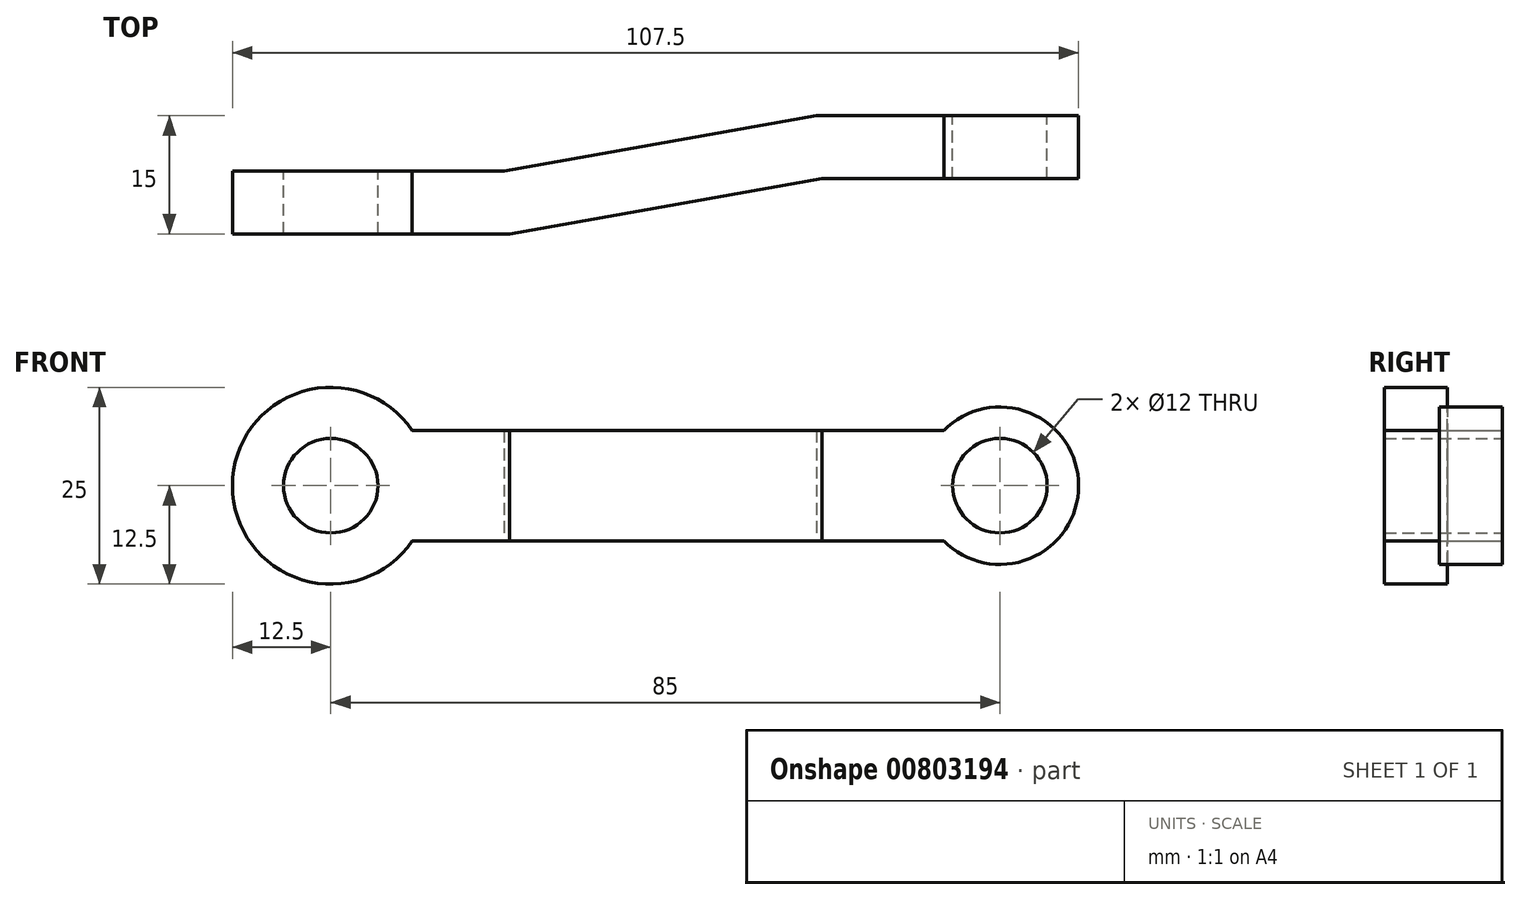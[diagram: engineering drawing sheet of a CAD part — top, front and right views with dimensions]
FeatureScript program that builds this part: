
annotation { "Feature Type Name" : "Feature", "Feature Type Description" : "" }
export const myFeature = defineFeature(function(context is Context, id is Id, definition is map)
    precondition{}
    {
        {
            var Q0;
            Q0=qCreatedBy(makeId("Front.planeOp"),FACE);
            var sketch = newSketch(context, id + "F0", { "sketchPlane" : qUnion([Q0])});
            skCircle(sketch, "E0", {"center": v(0, 0) * mm, "radius": 12.5 * mm});
            skCircle(sketch, "E1", {"center": v(85, 0) * mm, "radius": 10 * mm});
            skCircle(sketch, "E2", {"center": v(0, 0) * mm, "radius": 6 * mm});
            skCircle(sketch, "E3", {"center": v(85, 0) * mm, "radius": 6 * mm});
            skLineSegment(sketch, "E4", {"start": v(0, 0) * mm, "end": v(85, 0) * mm, "construction": true});
            skLineSegment(sketch, "E5", {"start": v(10.36, 7) * mm, "end": v(77.86, 7) * mm});
            skLineSegment(sketch, "E6.MirrorCS", {"start": v(10.36, -7) * mm, "end": v(77.86, -7) * mm});
            skSolve(sketch);
        }
        {
            var Q0;
            Q0 = qSketchRegion(id + "F0", true);
            extrude(context, id + "F1", {"entities" : qUnion([Q0]), "depth" : 20 * mm, "offsetDistance" : 25 * mm});
        }
        {
            var Q0;
            Q0=qCreatedBy(makeId("Top.planeOp"),FACE);
            var sketch = newSketch(context, id + "F2", { "sketchPlane" : qUnion([Q0])});
            skLineSegment(sketch, "E7", {"start": v(95, 0) * mm, "end": v(81.68, 0) * mm});
            skLineSegment(sketch, "E8", {"start": v(81.68, 0) * mm, "end": v(61.68, 0) * mm});
            skLineSegment(sketch, "E9", {"start": v(61.68, 0) * mm, "end": v(21.98, -7) * mm});
            skLineSegment(sketch, "E10", {"start": v(21.98, -7) * mm, "end": v(-12.5, -7) * mm});
            skLineSegment(sketch, "E11.0", {"start": v(22.68, -15) * mm, "end": v(-12.5, -15) * mm});
            skLineSegment(sketch, "E11.1", {"start": v(62.38, -8) * mm, "end": v(22.68, -15) * mm});
            skLineSegment(sketch, "E11.2", {"start": v(85.5, -8) * mm, "end": v(62.38, -8) * mm});
            skLineSegment(sketch, "E11.3", {"start": v(95, -8) * mm, "end": v(85.5, -8) * mm});
            skLineSegment(sketch, "E12", {"start": v(-12.5, -7) * mm, "end": v(-12.5, -15) * mm});
            skLineSegment(sketch, "E13", {"start": v(95, 0) * mm, "end": v(95, -8) * mm});
            skLineSegment(sketch, "E14", {"start": v(95, 0) * mm, "end": v(95, -20) * mm});
            skLineSegment(sketch, "E15", {"start": v(-12.5, -20) * mm, "end": v(-12.5, 0) * mm});
            skSolve(sketch);
        }
        {
            var Q0;
            Q0=makeQuery(id+"F2.imprint","IMPRINT",FACE,{"disambiguationData":[TD([[makeQuery(id+"F2.imprint","IMPRINT",EDGE,{"derivedFrom":sQuery(id+"F2.wireOp",EDGE,"E7")}),1.0]])]});
            extrude(context, id + "F3", {"entities" : qUnion([Q0]), "operationType" : NewBodyOperationType.INTERSECT, "endBound" : BoundingType.SYMMETRIC, "depth" : 25 * mm, "offsetDistance" : 25 * mm});
        }
    });
